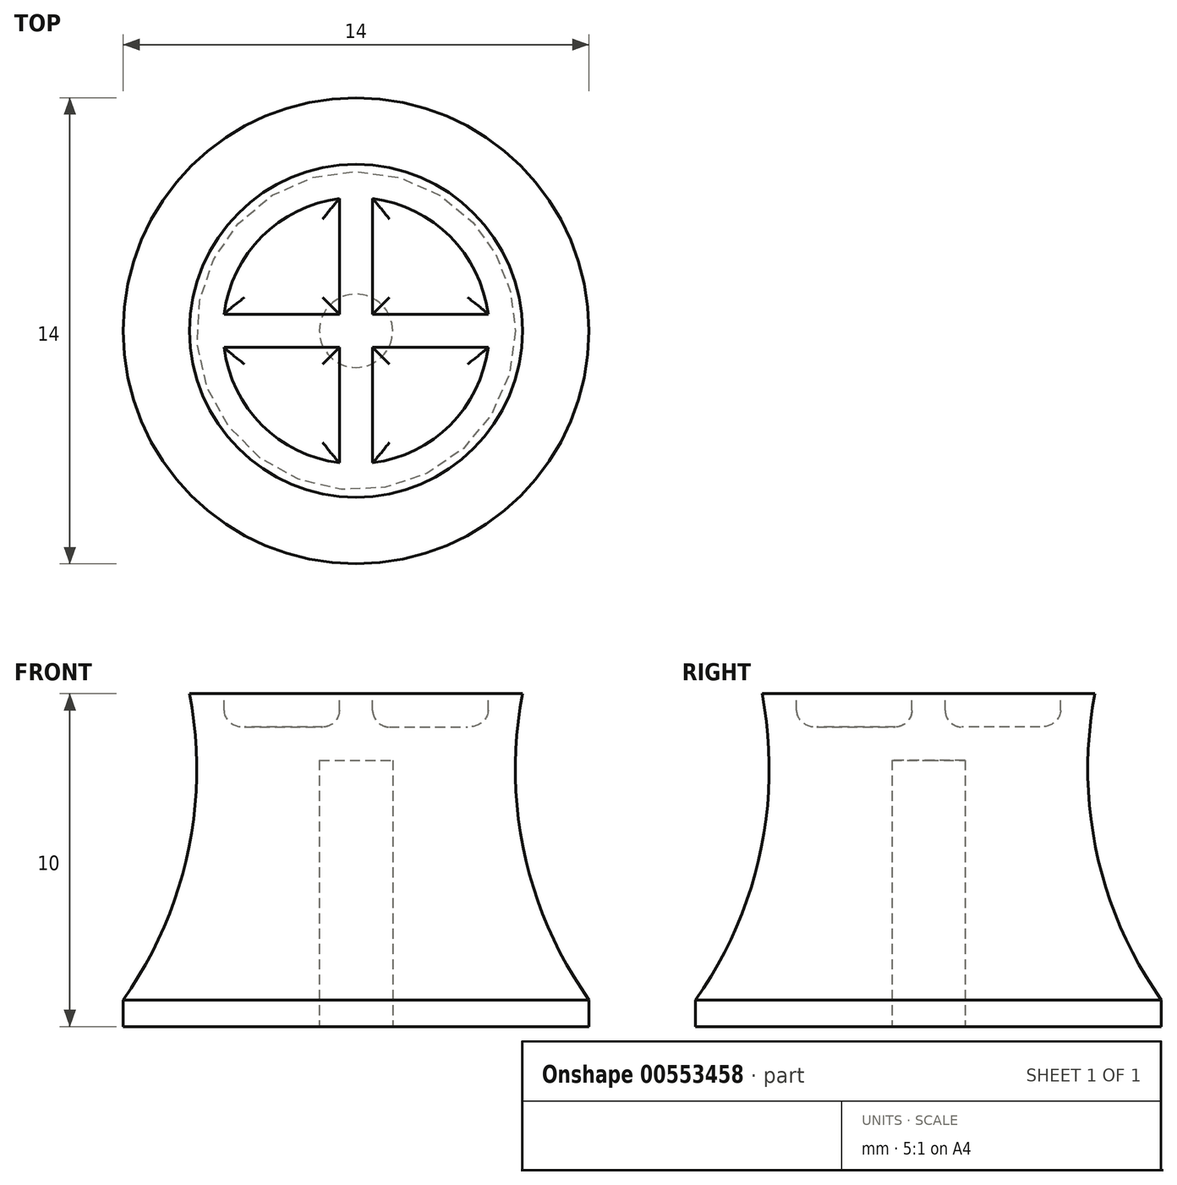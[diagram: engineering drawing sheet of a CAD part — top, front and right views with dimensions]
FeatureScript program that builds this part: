
annotation { "Feature Type Name" : "Feature", "Feature Type Description" : "" }
export const myFeature = defineFeature(function(context is Context, id is Id, definition is map)
    precondition{}
    {
        {
            var Q0;
            Q0=qCreatedBy(makeId("Right.planeOp"),FACE);
            var sketch = newSketch(context, id + "F0", { "sketchPlane" : qUnion([Q0])});
            skLineSegment(sketch, "E0", {"start": v(0, 0) * mm, "end": v(-7, 0) * mm});
            skLineSegment(sketch, "E1", {"start": v(0, 0) * mm, "end": v(0, 10) * mm});
            skLineSegment(sketch, "E2", {"start": v(0, 10) * mm, "end": v(-5, 10) * mm});
            skLineSegment(sketch, "E3", {"start": v(0, 24.51) * mm, "end": v(0, -9.99) * mm, "construction": true});
            skLineSegment(sketch, "E4", {"start": v(-7, 0) * mm, "end": v(-7, 0.8) * mm});
            skArc(sketch, "E5", {"start": v(-7, 0.8) * mm, "mid": v(-5.06, 5.2) * mm, "end": v(-5, 10) * mm});
            skSolve(sketch);
        }
        {
            var Q0;
            Q0 = qSketchRegion(id + "F0", true);
            var Q1;
            Q1=sQuery(id+"F0.wireOp",EDGE,"E3");
            revolve(context, id + "F1", {"entities" : qUnion([Q0]), "axis" : qUnion([Q1]), "revolveType" : RevolveType.FULL});
        }
        {
            var Q0;
            Q0=makeQuery(id+"F1.opRevolve","SWEPT_FACE",FACE,{"disambiguationData":[OSD([sQuery(id+"F0.wireOp",EDGE,"E0")])]});
            var sketch = newSketch(context, id + "F2", { "sketchPlane" : qUnion([Q0])});
            skCircle(sketch, "E6", {"center": v(0, 0) * mm, "radius": 1.1 * mm});
            skSolve(sketch);
        }
        {
            var Q0;
            Q0 = qSketchRegion(id + "F2", true);
            extrude(context, id + "F3", {"entities" : qUnion([Q0]), "operationType" : NewBodyOperationType.REMOVE, "oppositeDirection" : true, "depth" : 8 * mm, "offsetDistance" : 25 * mm});
        }
        {
            var Q0;
            Q0=makeQuery(id+"F1.opRevolve","SWEPT_FACE",FACE,{"disambiguationData":[OSD([sQuery(id+"F0.wireOp",EDGE,"E2")])]});
            var sketch = newSketch(context, id + "F4", { "sketchPlane" : qUnion([Q0])});
            skArc(sketch, "E7", {"start": v(-0.5, 3.97) * mm, "mid": v(-2.83, 2.83) * mm, "end": v(-3.97, 0.5) * mm});
            skLineSegment(sketch, "E8", {"start": v(0.5, 3.97) * mm, "end": v(0.5, 0.5) * mm});
            skLineSegment(sketch, "E9", {"start": v(-0.5, 3.97) * mm, "end": v(-0.5, 0.5) * mm});
            skLineSegment(sketch, "E10", {"start": v(-3.97, 0.5) * mm, "end": v(-0.5, 0.5) * mm});
            skLineSegment(sketch, "E11", {"start": v(-3.97, -0.5) * mm, "end": v(-0.5, -0.5) * mm});
            skArc(sketch, "E12.trimOffspring", {"start": v(-3.97, -0.5) * mm, "mid": v(-2.83, -2.83) * mm, "end": v(-0.5, -3.97) * mm});
            skArc(sketch, "E13.trimOffspring", {"start": v(0.5, -3.97) * mm, "mid": v(2.83, -2.83) * mm, "end": v(3.97, -0.5) * mm});
            skArc(sketch, "E14.trimOffspring", {"start": v(3.97, 0.5) * mm, "mid": v(2.83, 2.83) * mm, "end": v(0.5, 3.97) * mm});
            skLineSegment(sketch, "E15.trimOffspring", {"start": v(0.5, -0.5) * mm, "end": v(0.5, -3.97) * mm});
            skLineSegment(sketch, "E16.trimOffspring", {"start": v(0.5, 0.5) * mm, "end": v(3.97, 0.5) * mm});
            skLineSegment(sketch, "E17.trimOffspring", {"start": v(-0.5, -0.5) * mm, "end": v(-0.5, -3.97) * mm});
            skLineSegment(sketch, "E18.trimOffspring", {"start": v(0.5, -0.5) * mm, "end": v(3.97, -0.5) * mm});
            skSolve(sketch);
        }
        {
            var Q0;
            Q0 = qSketchRegion(id + "F4", true);
            extrude(context, id + "F5", {"entities" : qUnion([Q0]), "operationType" : NewBodyOperationType.REMOVE, "oppositeDirection" : true, "depth" : 1 * mm, "offsetDistance" : 25 * mm});
        }
        {
            var Q0;
            Q0=makeQuery(id+"F5.boolean.opBoolean","COPY",FACE,{"derivedFrom":makeQuery(id+"F5.opExtrude","CAP_FACE",FACE,{"disambiguationData":[OSD([sQuery(id+"F4.wireOp",EDGE,"E7"),sQuery(id+"F4.wireOp",EDGE,"E9"),sQuery(id+"F4.wireOp",EDGE,"E10")])],"isStart":false})});
            var Q1;
            Q1=makeQuery(id+"F5.boolean.opBoolean","COPY",FACE,{"derivedFrom":makeQuery(id+"F5.opExtrude","CAP_FACE",FACE,{"disambiguationData":[OSD([sQuery(id+"F4.wireOp",EDGE,"E8"),sQuery(id+"F4.wireOp",EDGE,"E14.trimOffspring"),sQuery(id+"F4.wireOp",EDGE,"E16.trimOffspring")])],"isStart":false})});
            var Q2;
            Q2=makeQuery(id+"F5.boolean.opBoolean","COPY",FACE,{"derivedFrom":makeQuery(id+"F5.opExtrude","CAP_FACE",FACE,{"disambiguationData":[OSD([sQuery(id+"F4.wireOp",EDGE,"E13.trimOffspring"),sQuery(id+"F4.wireOp",EDGE,"E15.trimOffspring"),sQuery(id+"F4.wireOp",EDGE,"E18.trimOffspring")])],"isStart":false})});
            var Q3;
            Q3=makeQuery(id+"F5.boolean.opBoolean","COPY",FACE,{"derivedFrom":makeQuery(id+"F5.opExtrude","CAP_FACE",FACE,{"disambiguationData":[OSD([sQuery(id+"F4.wireOp",EDGE,"E11"),sQuery(id+"F4.wireOp",EDGE,"E12.trimOffspring"),sQuery(id+"F4.wireOp",EDGE,"E17.trimOffspring")])],"isStart":false})});
            fillet(context, id + "F6", {"entities" : qUnion([Q0, Q1, Q2, Q3]), "radius" : 0.5 * mm, "tangentPropagation" : true, "allowEdgeOverflow" : false});
        }
    });
